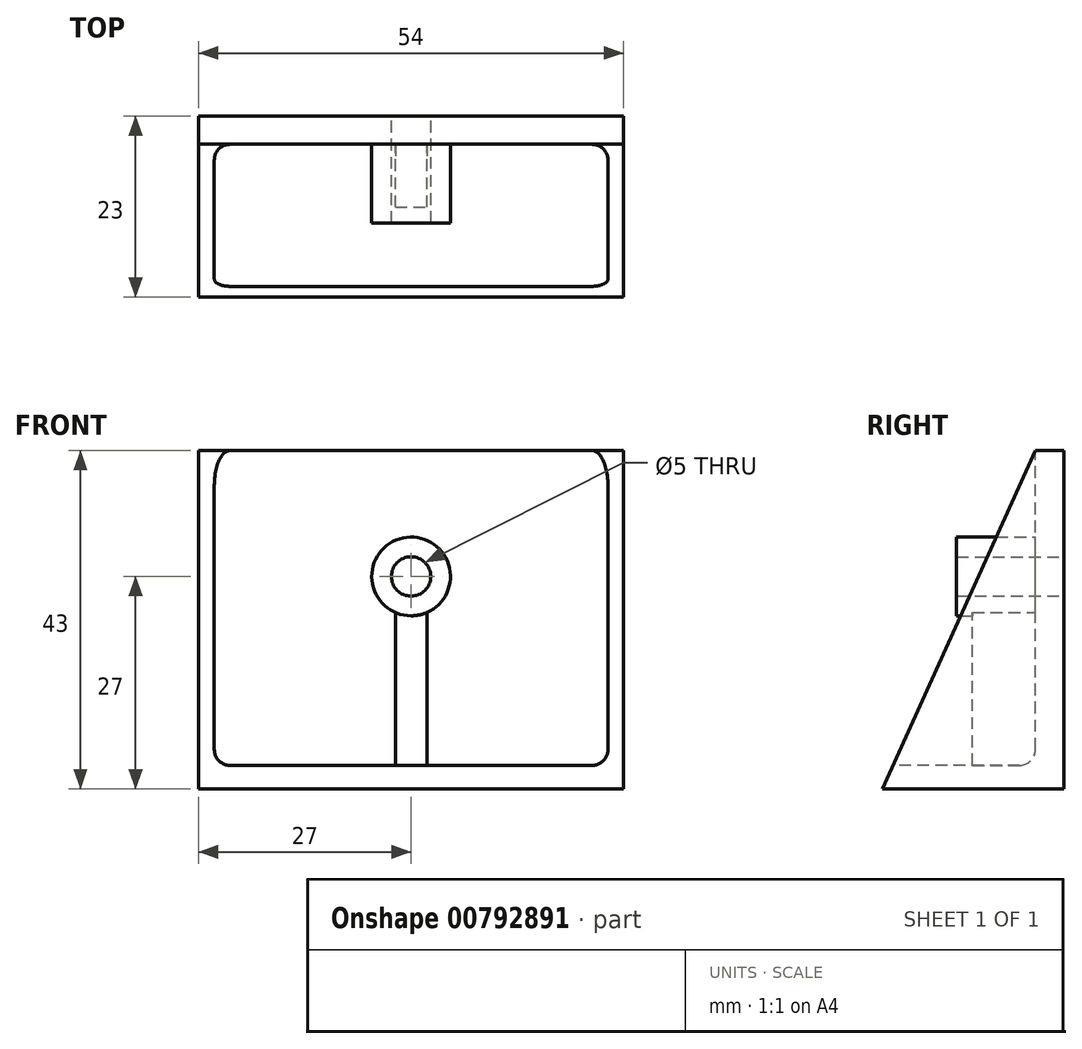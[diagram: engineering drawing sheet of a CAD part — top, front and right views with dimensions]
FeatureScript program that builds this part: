
annotation { "Feature Type Name" : "Feature", "Feature Type Description" : "" }
export const myFeature = defineFeature(function(context is Context, id is Id, definition is map)
    precondition{}
    {
        {
            var Q0;
            Q0=qCreatedBy(makeId("Right.planeOp"),FACE);
            var sketch = newSketch(context, id + "F0", { "sketchPlane" : qUnion([Q0])});
            skLineSegment(sketch, "E0", {"start": v(0, 0) * mm, "end": v(23, 0) * mm});
            skLineSegment(sketch, "E1", {"start": v(23, 43) * mm, "end": v(23, 0) * mm});
            skLineSegment(sketch, "E2", {"start": v(23, 43) * mm, "end": v(19.4, 43) * mm});
            skLineSegment(sketch, "E3", {"start": v(19.4, 43) * mm, "end": v(0, 0) * mm});
            skSolve(sketch);
        }
        {
            var Q0;
            Q0=makeQuery(id+"F0.imprint","IMPRINT",FACE,{"disambiguationData":[TD([[makeQuery(id+"F0.imprint","IMPRINT",EDGE,{"derivedFrom":sQuery(id+"F0.wireOp",EDGE,"E0")}),1.0]])]});
            extrude(context, id + "F1", {"entities" : qUnion([Q0]), "depth" : 54 * mm, "offsetDistance" : 25 * mm});
        }
        {
            var Q0;
            Q0=qCreatedBy(makeId("Top.planeOp"),FACE);
            cPlane(context, id + "F2", {"entities" : qUnion([Q0]), "cplaneType" : CPlaneType.OFFSET, "offset" : 43 * mm, "width" : 150 * mm, "height" : 150 * mm});
        }
        {
            var Q0;
            Q0=qCreatedBy(id+"F2.planeOp",FACE);
            var sketch = newSketch(context, id + "F3", { "sketchPlane" : qUnion([Q0])});
            skLineSegment(sketch, "E4.bottom", {"start": v(2, 19.4) * mm, "end": v(52, 19.4) * mm});
            skLineSegment(sketch, "E4.top", {"start": v(2, 0) * mm, "end": v(52, 0) * mm});
            skLineSegment(sketch, "E4.left", {"start": v(2, 19.4) * mm, "end": v(2, 0) * mm});
            skLineSegment(sketch, "E4.right", {"start": v(52, 19.4) * mm, "end": v(52, 0) * mm});
            skSolve(sketch);
        }
        {
            var Q0;
            Q0=makeQuery(id+"F3.imprint","IMPRINT",FACE,{"disambiguationData":[TD([[makeQuery(id+"F3.imprint","IMPRINT",EDGE,{"derivedFrom":sQuery(id+"F3.wireOp",EDGE,"E4.bottom")}),-1.0]])]});
            extrude(context, id + "F4", {"entities" : qUnion([Q0]), "operationType" : NewBodyOperationType.REMOVE, "oppositeDirection" : true, "depth" : 40 * mm, "offsetDistance" : 25 * mm});
        }
        {
            var Q0;
            Q0=makeQuery(id+"F4.boolean.opBoolean","COPY",FACE,{"derivedFrom":makeQuery(id+"F4.opExtrude","SWEPT_FACE",FACE,{"disambiguationData":[OSD([sQuery(id+"F3.wireOp",EDGE,"E4.bottom")])]})});
            var sketch = newSketch(context, id + "F5", { "sketchPlane" : qUnion([Q0])});
            skCircle(sketch, "E5", {"center": v(27, 27) * mm, "radius": 5 * mm});
            skLineSegment(sketch, "E6", {"start": v(25, 3) * mm, "end": v(25, 22.42) * mm});
            skLineSegment(sketch, "E7", {"start": v(29, 3) * mm, "end": v(29, 22.42) * mm});
            skSolve(sketch);
        }
        {
            var Q0;
            {var subQ0=sQuery(id+"F5.wireOp",EDGE,"E6");Q0=makeQuery(id+"F5.imprint","IMPRINT",FACE,{"disambiguationData":[TD([[makeQuery(id+"F5.imprint","IMPRINT",EDGE,{"derivedFrom":subQ0}),-1.0]])]});}
            extrude(context, id + "F6", {"entities" : qUnion([Q0]), "operationType" : NewBodyOperationType.ADD, "depth" : 8 * mm, "offsetDistance" : 25 * mm});
        }
        {
            var Q0;
            Q0=makeQuery(id+"F4.boolean.opBoolean","COPY",FACE,{"derivedFrom":makeQuery(id+"F4.opExtrude","SWEPT_FACE",FACE,{"disambiguationData":[OSD([sQuery(id+"F3.wireOp",EDGE,"E4.bottom")])]})});
            var sketch = newSketch(context, id + "F7", { "sketchPlane" : qUnion([Q0])});
            skCircle(sketch, "E8", {"center": v(27, 27) * mm, "radius": 5 * mm});
            skLineSegment(sketch, "E9", {"start": v(25, 3) * mm, "end": v(25, 22.42) * mm});
            skLineSegment(sketch, "E10", {"start": v(29, 3) * mm, "end": v(29, 22.42) * mm});
            skSolve(sketch);
        }
        {
            var Q0;
            {var subQ0=sQuery(id+"F7.wireOp",EDGE,"E8");var subQ1=makeQuery(id+"F7.imprint","INTERSECT",VERTEX,{"derivedFrom":[subQ0,sQuery(id+"F7.wireOp",EDGE,"E9")]});Q0=makeQuery(id+"F7.imprint","IMPRINT",FACE,{"disambiguationData":[TD([[makeQuery(id+"F7.imprint","IMPRINT",EDGE,{"disambiguationData":[TD([[subQ1,-1.0]])],"derivedFrom":subQ0}),1.0]])]});}
            extrude(context, id + "F8", {"entities" : qUnion([Q0]), "operationType" : NewBodyOperationType.ADD, "depth" : 10 * mm, "offsetDistance" : 25 * mm});
        }
        {
            var Q0;
            Q0=makeQuery(id+"F1.opExtrude","SWEPT_FACE",FACE,{"disambiguationData":[OSD([sQuery(id+"F0.wireOp",EDGE,"E1")])]});
            var sketch = newSketch(context, id + "F9", { "sketchPlane" : qUnion([Q0])});
            skPoint(sketch, "E11", {"position": v(-27, 27) * mm});
            skSolve(sketch);
        }
        {
            var Q0;
            Q0=sQuery(id+"F9.wireOp",VERTEX,"E11");
            var Q1;
            Q1=makeQuery(id+"F1.opExtrude","SWEPT_BODY",BODY,{"disambiguationData":[OSD([sQuery(id+"F0.wireOp",EDGE,"E0"),sQuery(id+"F0.wireOp",EDGE,"E1"),sQuery(id+"F0.wireOp",EDGE,"E2"),sQuery(id+"F0.wireOp",EDGE,"E3")])]});
            hole(context, id + "F10", {"style" : HoleStyle.SIMPLE, "endStyle" : HoleEndStyle.THROUGH, "holeDiameter" : 5 * mm, "majorDiameter" : 5 * mm, "isTappedThrough" : true, "tappedDepth" : 12 * mm, "tapClearance" : 3, "locations" : qUnion([Q0]), "scope" : qUnion([Q1])});
        }
        {
            var Q0;
            Q0=makeQuery(id+"F4.boolean.opBoolean","COPY",EDGE,{"derivedFrom":makeQuery(id+"F4.opExtrude","SWEPT_EDGE",EDGE,{"disambiguationData":[OSD([sQuery(id+"F3.wireOp",EDGE,"E4.bottom"),sQuery(id+"F3.wireOp",EDGE,"E4.left")])]})});
            var Q1;
            {var subQ0=sQuery(id+"F3.wireOp",EDGE,"E4.bottom");var subQ1=sQuery(id+"F3.wireOp",EDGE,"E4.left");Q1=makeQuery(id+"F6.boolean.opBoolean","SPLIT",EDGE,{"disambiguationData":[TD([makeQuery(id+"F4.boolean.opBoolean","COPY",FACE,{"derivedFrom":makeQuery(id+"F4.opExtrude","SWEPT_FACE",FACE,{"disambiguationData":[OSD([subQ1])]})})])],"derivedFrom":makeQuery(id+"F4.boolean.opBoolean","COPY",EDGE,{"derivedFrom":makeQuery(id+"F4.opExtrude","CAP_EDGE",EDGE,{"disambiguationData":[OSD([subQ0])],"isStart":false})})});}
            var Q2;
            Q2=makeQuery(id+"F4.boolean.opBoolean","COPY",EDGE,{"derivedFrom":makeQuery(id+"F4.opExtrude","CAP_EDGE",EDGE,{"disambiguationData":[OSD([sQuery(id+"F3.wireOp",EDGE,"E4.left")])],"isStart":false})});
            var Q3;
            Q3=makeQuery(id+"F6.opExtrude","SWEPT_EDGE",EDGE,{"disambiguationData":[OSD([sQuery(id+"F3.wireOp",EDGE,"E4.bottom"),sQuery(id+"F5.wireOp",EDGE,"E7")])]});
            var Q4;
            Q4=makeQuery(id+"F6.opExtrude","CAP_EDGE",EDGE,{"disambiguationData":[OSD([sQuery(id+"F3.wireOp",EDGE,"E4.bottom")])],"isStart":false});
            var Q5;
            {var subQ0=sQuery(id+"F3.wireOp",EDGE,"E4.bottom");var subQ1=sQuery(id+"F3.wireOp",EDGE,"E4.right");Q5=makeQuery(id+"F6.boolean.opBoolean","SPLIT",EDGE,{"disambiguationData":[TD([makeQuery(id+"F4.boolean.opBoolean","COPY",FACE,{"derivedFrom":makeQuery(id+"F4.opExtrude","SWEPT_FACE",FACE,{"disambiguationData":[OSD([subQ1])]})})])],"derivedFrom":makeQuery(id+"F4.boolean.opBoolean","COPY",EDGE,{"derivedFrom":makeQuery(id+"F4.opExtrude","CAP_EDGE",EDGE,{"disambiguationData":[OSD([subQ0])],"isStart":false})})});}
            var Q6;
            Q6=makeQuery(id+"F8.opExtrude","CAP_EDGE",EDGE,{"disambiguationData":[OSD([sQuery(id+"F7.wireOp",EDGE,"E8")])],"isStart":true});
            var Q7;
            Q7=makeQuery(id+"F6.opExtrude","CAP_EDGE",EDGE,{"disambiguationData":[OSD([sQuery(id+"F5.wireOp",EDGE,"E6")])],"isStart":true});
            var Q8;
            Q8=makeQuery(id+"F6.opExtrude","SWEPT_EDGE",EDGE,{"disambiguationData":[OSD([sQuery(id+"F5.wireOp",EDGE,"E5"),sQuery(id+"F5.wireOp",EDGE,"E6")])]});
            var Q9;
            Q9=makeQuery(id+"F6.opExtrude","SWEPT_EDGE",EDGE,{"disambiguationData":[OSD([sQuery(id+"F3.wireOp",EDGE,"E4.bottom"),sQuery(id+"F5.wireOp",EDGE,"E6")])]});
            var Q10;
            Q10=makeQuery(id+"F4.boolean.opBoolean","COPY",EDGE,{"derivedFrom":makeQuery(id+"F4.opExtrude","CAP_EDGE",EDGE,{"disambiguationData":[OSD([sQuery(id+"F3.wireOp",EDGE,"E4.right")])],"isStart":false})});
            var Q11;
            Q11=makeQuery(id+"F4.boolean.opBoolean","COPY",EDGE,{"derivedFrom":makeQuery(id+"F4.opExtrude","SWEPT_EDGE",EDGE,{"disambiguationData":[OSD([sQuery(id+"F3.wireOp",EDGE,"E4.bottom"),sQuery(id+"F3.wireOp",EDGE,"E4.right")])]})});
            var Q12;
            Q12=makeQuery(id+"F6.opExtrude","SWEPT_EDGE",EDGE,{"disambiguationData":[OSD([sQuery(id+"F5.wireOp",EDGE,"E5"),sQuery(id+"F5.wireOp",EDGE,"E7")])]});
            var Q13;
            Q13=makeQuery(id+"F6.opExtrude","CAP_EDGE",EDGE,{"disambiguationData":[OSD([sQuery(id+"F5.wireOp",EDGE,"E7")])],"isStart":true});
            fillet(context, id + "F11", {"entities" : qUnion([Q0, Q1, Q2, Q3, Q4, Q5, Q6, Q7, Q8, Q9, Q10, Q11, Q12, Q13]), "radius" : 2 * mm, "tangentPropagation" : true, "allowEdgeOverflow" : false});
        }
    });
